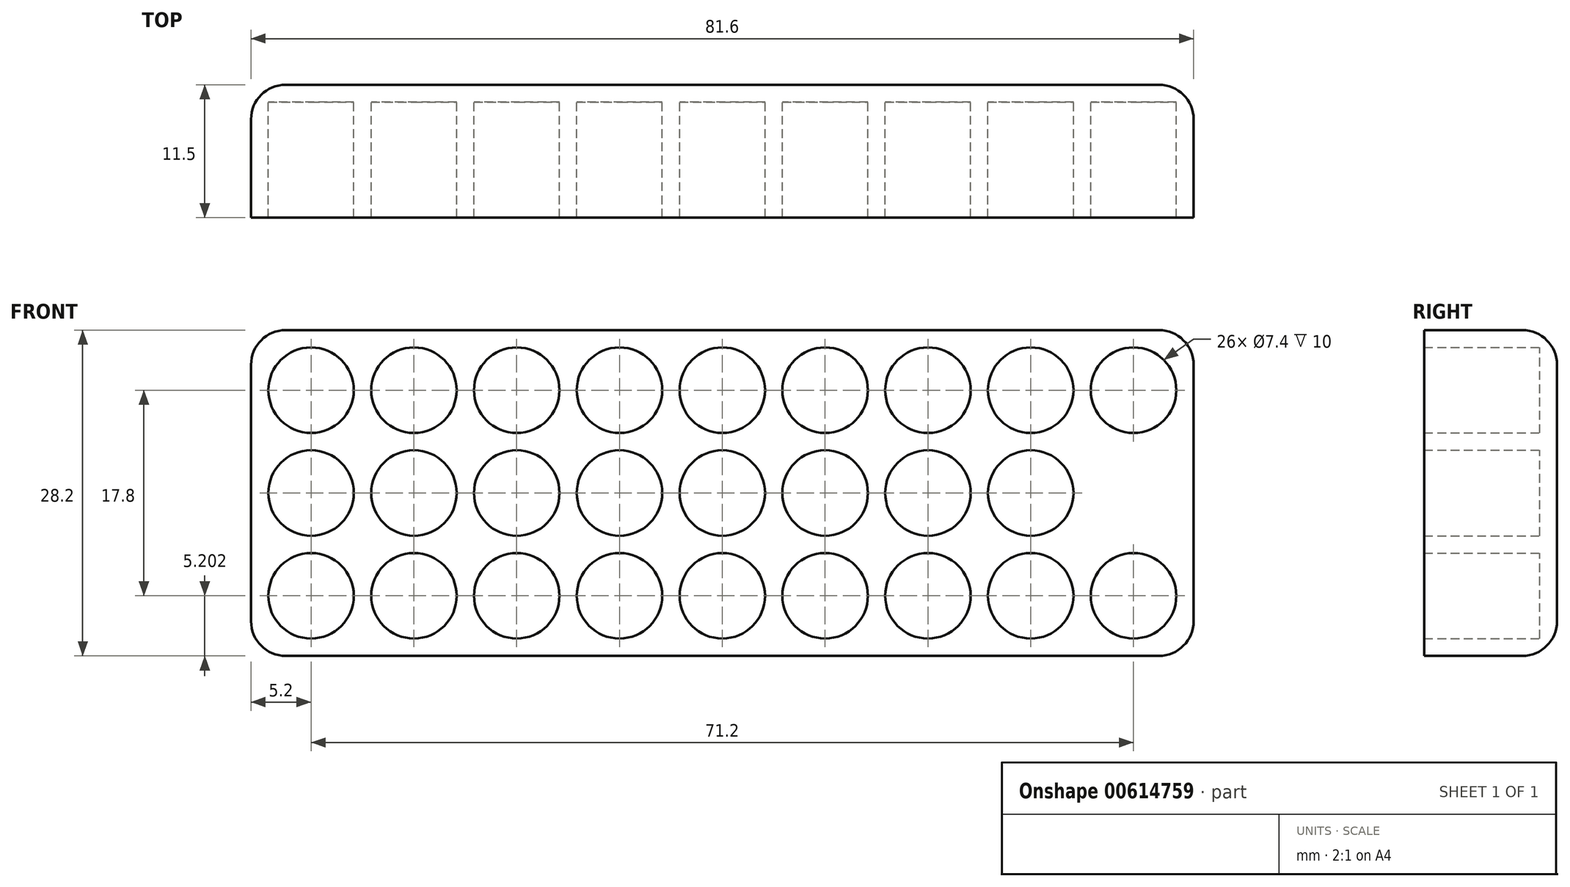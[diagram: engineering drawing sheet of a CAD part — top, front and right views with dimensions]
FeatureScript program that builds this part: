
annotation { "Feature Type Name" : "Feature", "Feature Type Description" : "" }
export const myFeature = defineFeature(function(context is Context, id is Id, definition is map)
    precondition{}
    {
        {
            var Q0;
            Q0=qCreatedBy(makeId("Front.planeOp"),FACE);
            var sketch = newSketch(context, id + "F0", { "sketchPlane" : qUnion([Q0])});
            skLineSegment(sketch, "E0.bottom", {"start": v(-44.48, 59.11) * mm, "end": v(37.12, 59.11) * mm});
            skLineSegment(sketch, "E0.top", {"start": v(-44.48, 30.91) * mm, "end": v(37.12, 30.91) * mm});
            skLineSegment(sketch, "E0.left", {"start": v(-44.48, 59.11) * mm, "end": v(-44.48, 30.91) * mm});
            skLineSegment(sketch, "E0.right", {"start": v(37.12, 59.11) * mm, "end": v(37.12, 30.91) * mm});
            skCircle(sketch, "E1", {"center": v(31.92, 53.91) * mm, "radius": 3.7 * mm});
            skCircle(sketch, "E2", {"center": v(23.02, 53.91) * mm, "radius": 3.7 * mm});
            skCircle(sketch, "E3", {"center": v(14.12, 53.91) * mm, "radius": 3.7 * mm});
            skCircle(sketch, "E4", {"center": v(5.22, 53.91) * mm, "radius": 3.7 * mm});
            skCircle(sketch, "E5", {"center": v(-3.68, 53.91) * mm, "radius": 3.7 * mm});
            skCircle(sketch, "E6", {"center": v(-12.58, 53.91) * mm, "radius": 3.7 * mm});
            skCircle(sketch, "E7", {"center": v(-21.48, 53.91) * mm, "radius": 3.7 * mm});
            skCircle(sketch, "E8", {"center": v(-30.38, 53.91) * mm, "radius": 3.7 * mm});
            skCircle(sketch, "E9", {"center": v(-39.28, 53.91) * mm, "radius": 3.7 * mm});
            skCircle(sketch, "E10", {"center": v(31.92, 45.01) * mm, "radius": 3.7 * mm});
            skCircle(sketch, "E11", {"center": v(23.02, 45.01) * mm, "radius": 3.7 * mm});
            skCircle(sketch, "E12", {"center": v(14.12, 45.01) * mm, "radius": 3.7 * mm});
            skCircle(sketch, "E13", {"center": v(5.22, 45.01) * mm, "radius": 3.7 * mm});
            skCircle(sketch, "E14", {"center": v(-3.68, 45.01) * mm, "radius": 3.7 * mm});
            skCircle(sketch, "E15", {"center": v(-12.58, 45.01) * mm, "radius": 3.7 * mm});
            skCircle(sketch, "E16", {"center": v(-21.48, 45.01) * mm, "radius": 3.7 * mm});
            skCircle(sketch, "E17", {"center": v(-30.38, 45.01) * mm, "radius": 3.7 * mm});
            skCircle(sketch, "E18", {"center": v(-39.28, 45.01) * mm, "radius": 3.7 * mm});
            skCircle(sketch, "E19", {"center": v(31.92, 36.11) * mm, "radius": 3.7 * mm});
            skCircle(sketch, "E20", {"center": v(23.02, 36.11) * mm, "radius": 3.7 * mm});
            skCircle(sketch, "E21", {"center": v(14.12, 36.11) * mm, "radius": 3.7 * mm});
            skCircle(sketch, "E22", {"center": v(5.22, 36.11) * mm, "radius": 3.7 * mm});
            skCircle(sketch, "E23", {"center": v(-3.68, 36.11) * mm, "radius": 3.7 * mm});
            skCircle(sketch, "E24", {"center": v(-12.58, 36.11) * mm, "radius": 3.7 * mm});
            skCircle(sketch, "E25", {"center": v(-21.48, 36.11) * mm, "radius": 3.7 * mm});
            skCircle(sketch, "E26", {"center": v(-30.38, 36.11) * mm, "radius": 3.7 * mm});
            skCircle(sketch, "E27", {"center": v(-39.28, 36.11) * mm, "radius": 3.7 * mm});
            skSolve(sketch);
        }
        {
            var Q0;
            Q0=makeQuery(id+"F0.imprint","IMPRINT",FACE,{"disambiguationData":[TD([[makeQuery(id+"F0.imprint","IMPRINT",EDGE,{"derivedFrom":sQuery(id+"F0.wireOp",EDGE,"E0.bottom")}),-1.0]])]});
            var Q1;
            Q1=makeQuery(id+"F0.imprint","IMPRINT",FACE,{"disambiguationData":[TD([[makeQuery(id+"F0.imprint","IMPRINT",EDGE,{"derivedFrom":sQuery(id+"F0.wireOp",EDGE,"E10")}),1.0]])]});
            extrude(context, id + "F1", {"entities" : qUnion([Q0, Q1]), "depth" : 10 * mm, "offsetDistance" : 25 * mm});
        }
        {
            var Q0;
            Q0=makeQuery(id+"F1.opExtrude","CAP_FACE",FACE,{"disambiguationData":[OSD([sQuery(id+"F0.wireOp",EDGE,"E0.bottom"),sQuery(id+"F0.wireOp",EDGE,"E0.top"),sQuery(id+"F0.wireOp",EDGE,"E0.left"),sQuery(id+"F0.wireOp",EDGE,"E0.right"),sQuery(id+"F0.wireOp",EDGE,"E1"),sQuery(id+"F0.wireOp",EDGE,"E2"),sQuery(id+"F0.wireOp",EDGE,"E3"),sQuery(id+"F0.wireOp",EDGE,"E4"),sQuery(id+"F0.wireOp",EDGE,"E5"),sQuery(id+"F0.wireOp",EDGE,"E6"),sQuery(id+"F0.wireOp",EDGE,"E7"),sQuery(id+"F0.wireOp",EDGE,"E8"),sQuery(id+"F0.wireOp",EDGE,"E9"),sQuery(id+"F0.wireOp",EDGE,"E11"),sQuery(id+"F0.wireOp",EDGE,"E12"),sQuery(id+"F0.wireOp",EDGE,"E13"),sQuery(id+"F0.wireOp",EDGE,"E14"),sQuery(id+"F0.wireOp",EDGE,"E15"),sQuery(id+"F0.wireOp",EDGE,"E16"),sQuery(id+"F0.wireOp",EDGE,"E17"),sQuery(id+"F0.wireOp",EDGE,"E18"),sQuery(id+"F0.wireOp",EDGE,"E19"),sQuery(id+"F0.wireOp",EDGE,"E20"),sQuery(id+"F0.wireOp",EDGE,"E21"),sQuery(id+"F0.wireOp",EDGE,"E22"),sQuery(id+"F0.wireOp",EDGE,"E23"),sQuery(id+"F0.wireOp",EDGE,"E24"),sQuery(id+"F0.wireOp",EDGE,"E25"),sQuery(id+"F0.wireOp",EDGE,"E26"),sQuery(id+"F0.wireOp",EDGE,"E27")])],"isStart":true});
            var sketch = newSketch(context, id + "F2", { "sketchPlane" : qUnion([Q0])});
            skLineSegment(sketch, "E28.bottom", {"start": v(-37.12, 59.11) * mm, "end": v(44.48, 59.11) * mm});
            skLineSegment(sketch, "E28.top", {"start": v(-37.12, 30.91) * mm, "end": v(44.48, 30.91) * mm});
            skLineSegment(sketch, "E28.left", {"start": v(-37.12, 59.11) * mm, "end": v(-37.12, 30.91) * mm});
            skLineSegment(sketch, "E28.right", {"start": v(44.48, 59.11) * mm, "end": v(44.48, 30.91) * mm});
            skSolve(sketch);
        }
        {
            var Q0;
            Q0 = qSketchRegion(id + "F2", true);
            extrude(context, id + "F3", {"entities" : qUnion([Q0]), "operationType" : NewBodyOperationType.ADD, "depth" : 1.5 * mm, "offsetDistance" : 25 * mm});
        }
        {
            var Q0;
            Q0=makeQuery(id+"F3.boolean.opBoolean","MERGE",EDGE,{"derivedFrom":[makeQuery(id+"F1.opExtrude","SWEPT_EDGE",EDGE,{"disambiguationData":[OSD([sQuery(id+"F0.wireOp",EDGE,"E0.top"),sQuery(id+"F0.wireOp",EDGE,"E0.left")])]}),makeQuery(id+"F3.opExtrude","SWEPT_EDGE",EDGE,{"disambiguationData":[OSD([sQuery(id+"F2.wireOp",EDGE,"E28.top"),sQuery(id+"F2.wireOp",EDGE,"E28.right")])]})]});
            var Q1;
            Q1=makeQuery(id+"F3.boolean.opBoolean","MERGE",EDGE,{"derivedFrom":[makeQuery(id+"F1.opExtrude","SWEPT_EDGE",EDGE,{"disambiguationData":[OSD([sQuery(id+"F0.wireOp",EDGE,"E0.bottom"),sQuery(id+"F0.wireOp",EDGE,"E0.left")])]}),makeQuery(id+"F3.opExtrude","SWEPT_EDGE",EDGE,{"disambiguationData":[OSD([sQuery(id+"F2.wireOp",EDGE,"E28.bottom"),sQuery(id+"F2.wireOp",EDGE,"E28.right")])]})]});
            var Q2;
            Q2=makeQuery(id+"F3.boolean.opBoolean","MERGE",EDGE,{"derivedFrom":[makeQuery(id+"F1.opExtrude","SWEPT_EDGE",EDGE,{"disambiguationData":[OSD([sQuery(id+"F0.wireOp",EDGE,"E0.top"),sQuery(id+"F0.wireOp",EDGE,"E0.right")])]}),makeQuery(id+"F3.opExtrude","SWEPT_EDGE",EDGE,{"disambiguationData":[OSD([sQuery(id+"F2.wireOp",EDGE,"E28.top"),sQuery(id+"F2.wireOp",EDGE,"E28.left")])]})]});
            var Q3;
            Q3=makeQuery(id+"F3.boolean.opBoolean","MERGE",EDGE,{"derivedFrom":[makeQuery(id+"F1.opExtrude","SWEPT_EDGE",EDGE,{"disambiguationData":[OSD([sQuery(id+"F0.wireOp",EDGE,"E0.bottom"),sQuery(id+"F0.wireOp",EDGE,"E0.right")])]}),makeQuery(id+"F3.opExtrude","SWEPT_EDGE",EDGE,{"disambiguationData":[OSD([sQuery(id+"F2.wireOp",EDGE,"E28.bottom"),sQuery(id+"F2.wireOp",EDGE,"E28.left")])]})]});
            var Q4;
            Q4=makeQuery(id+"F3.opExtrude","CAP_FACE",FACE,{"disambiguationData":[OSD([sQuery(id+"F2.wireOp",EDGE,"E28.bottom"),sQuery(id+"F2.wireOp",EDGE,"E28.top"),sQuery(id+"F2.wireOp",EDGE,"E28.left"),sQuery(id+"F2.wireOp",EDGE,"E28.right")])],"isStart":false});
            fillet(context, id + "F4", {"entities" : qUnion([Q0, Q1, Q2, Q3, Q4]), "tangentPropagation" : true, "radius" : 3 * mm, "defaultsChanged" : true, "vertexSettings" : [], "allowEdgeOverflow" : false});
        }
    });
